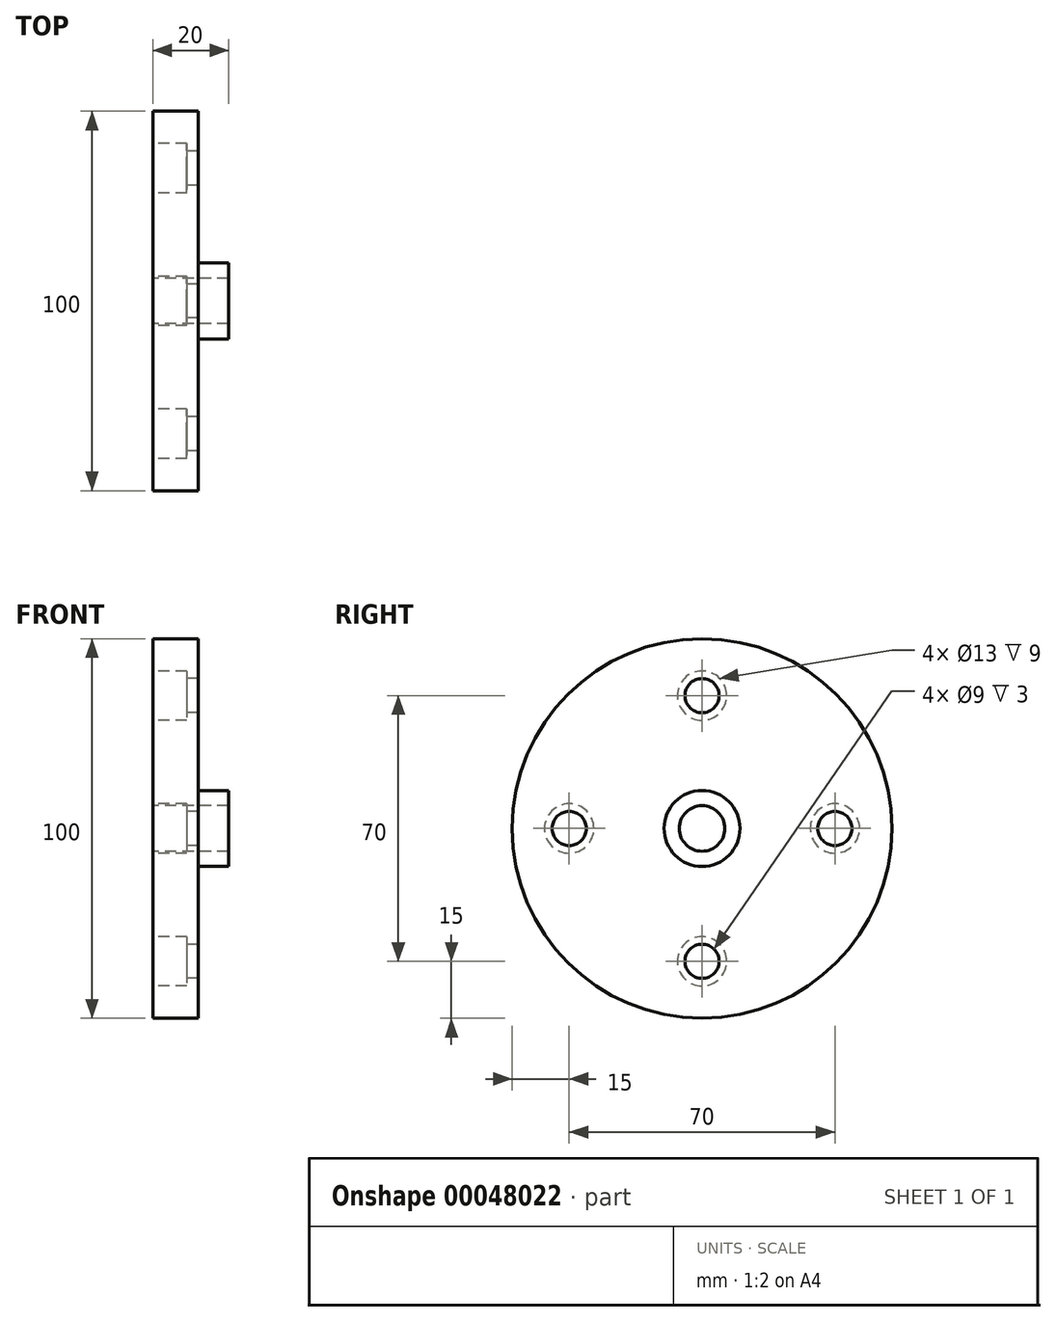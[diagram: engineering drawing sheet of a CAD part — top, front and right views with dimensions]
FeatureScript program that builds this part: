
annotation { "Feature Type Name" : "Feature", "Feature Type Description" : "" }
export const myFeature = defineFeature(function(context is Context, id is Id, definition is map)
    precondition{}
    {
        {
            var Q0;
            Q0=qCreatedBy(makeId("Front.planeOp"),FACE);
            var sketch = newSketch(context, id + "F0", { "sketchPlane" : qUnion([Q0])});
            skLineSegment(sketch, "E0", {"start": v(0, 6) * mm, "end": v(0, 50) * mm});
            skLineSegment(sketch, "E1", {"start": v(0, 50) * mm, "end": v(12, 50) * mm});
            skLineSegment(sketch, "E2", {"start": v(12, 50) * mm, "end": v(12, 10) * mm});
            skLineSegment(sketch, "E3", {"start": v(12, 10) * mm, "end": v(20, 10) * mm});
            skLineSegment(sketch, "E4", {"start": v(20, 10) * mm, "end": v(20, 6) * mm});
            skLineSegment(sketch, "E5", {"start": v(20, 6) * mm, "end": v(0, 6) * mm});
            skLineSegment(sketch, "E6", {"start": v(0, 0) * mm, "end": v(53.18, 0) * mm, "construction": true});
            skSolve(sketch);
        }
        {
            var Q0;
            Q0=makeQuery(id+"F0.imprint","IMPRINT",FACE,{"disambiguationData":[TD([[makeQuery(id+"F0.imprint","IMPRINT",EDGE,{"derivedFrom":sQuery(id+"F0.wireOp",EDGE,"E0")}),-1.0]])]});
            var Q1;
            Q1=sQuery(id+"F0.wireOp",EDGE,"E6");
            revolve(context, id + "F1", {"entities" : qUnion([Q0]), "axis" : qUnion([Q1]), "revolveType" : RevolveType.FULL});
        }
        {
            var Q0;
            Q0=makeQuery(id+"F1.opRevolve","SWEPT_FACE",FACE,{"disambiguationData":[OSD([sQuery(id+"F0.wireOp",EDGE,"E0")])]});
            var sketch = newSketch(context, id + "F2", { "sketchPlane" : qUnion([Q0])});
            skCircle(sketch, "E7", {"center": v(0, 35) * mm, "radius": 6.5 * mm});
            skCircle(sketch, "E8.1.0", {"center": v(-35, 0) * mm, "radius": 6.5 * mm});
            skCircle(sketch, "E8.2.0", {"center": v(0, -35) * mm, "radius": 6.5 * mm});
            skCircle(sketch, "E8.3.0", {"center": v(35, 0) * mm, "radius": 6.5 * mm});
            skPoint(sketch, "E8.center", {"position": v(0, 0) * mm});
            skCircle(sketch, "E9", {"center": v(0, 35) * mm, "radius": 4.5 * mm});
            skCircle(sketch, "E10.1.0", {"center": v(-35, 0) * mm, "radius": 4.5 * mm});
            skCircle(sketch, "E10.2.0", {"center": v(0, -35) * mm, "radius": 4.5 * mm});
            skCircle(sketch, "E10.3.0", {"center": v(35, 0) * mm, "radius": 4.5 * mm});
            skSolve(sketch);
        }
        {
            var Q0;
            Q0 = qSketchRegion(id + "F2", true);
            extrude(context, id + "F3", {"entities" : qUnion([Q0]), "operationType" : NewBodyOperationType.REMOVE, "oppositeDirection" : true, "depth" : 9 * mm});
        }
        {
            var Q0;
            Q0=makeQuery(id+"F3.boolean.opBoolean","SPLIT",FACE,{"disambiguationData":[TD([makeQuery(id+"F3.opExtrude","SWEPT_FACE",FACE,{"disambiguationData":[OSD([sQuery(id+"F2.wireOp",EDGE,"E9")])]})])],"derivedFrom":makeQuery(id+"F1.opRevolve","SWEPT_FACE",FACE,{"disambiguationData":[OSD([sQuery(id+"F0.wireOp",EDGE,"E0")])]})});
            var Q1;
            Q1=makeQuery(id+"F3.boolean.opBoolean","SPLIT",FACE,{"disambiguationData":[TD([makeQuery(id+"F3.opExtrude","SWEPT_FACE",FACE,{"disambiguationData":[OSD([sQuery(id+"F2.wireOp",EDGE,"E10.1.0")])]})])],"derivedFrom":makeQuery(id+"F1.opRevolve","SWEPT_FACE",FACE,{"disambiguationData":[OSD([sQuery(id+"F0.wireOp",EDGE,"E0")])]})});
            var Q2;
            Q2=makeQuery(id+"F3.boolean.opBoolean","SPLIT",FACE,{"disambiguationData":[TD([makeQuery(id+"F3.opExtrude","SWEPT_FACE",FACE,{"disambiguationData":[OSD([sQuery(id+"F2.wireOp",EDGE,"E10.2.0")])]})])],"derivedFrom":makeQuery(id+"F1.opRevolve","SWEPT_FACE",FACE,{"disambiguationData":[OSD([sQuery(id+"F0.wireOp",EDGE,"E0")])]})});
            var Q3;
            Q3=makeQuery(id+"F3.boolean.opBoolean","SPLIT",FACE,{"disambiguationData":[TD([makeQuery(id+"F3.opExtrude","SWEPT_FACE",FACE,{"disambiguationData":[OSD([sQuery(id+"F2.wireOp",EDGE,"E10.3.0")])]})])],"derivedFrom":makeQuery(id+"F1.opRevolve","SWEPT_FACE",FACE,{"disambiguationData":[OSD([sQuery(id+"F0.wireOp",EDGE,"E0")])]})});
            extrude(context, id + "F4", {"entities" : qUnion([Q0, Q1, Q2, Q3]), "operationType" : NewBodyOperationType.REMOVE, "endBound" : BoundingType.THROUGH_ALL, "oppositeDirection" : true, "depth" : 25 * mm});
        }
    });
